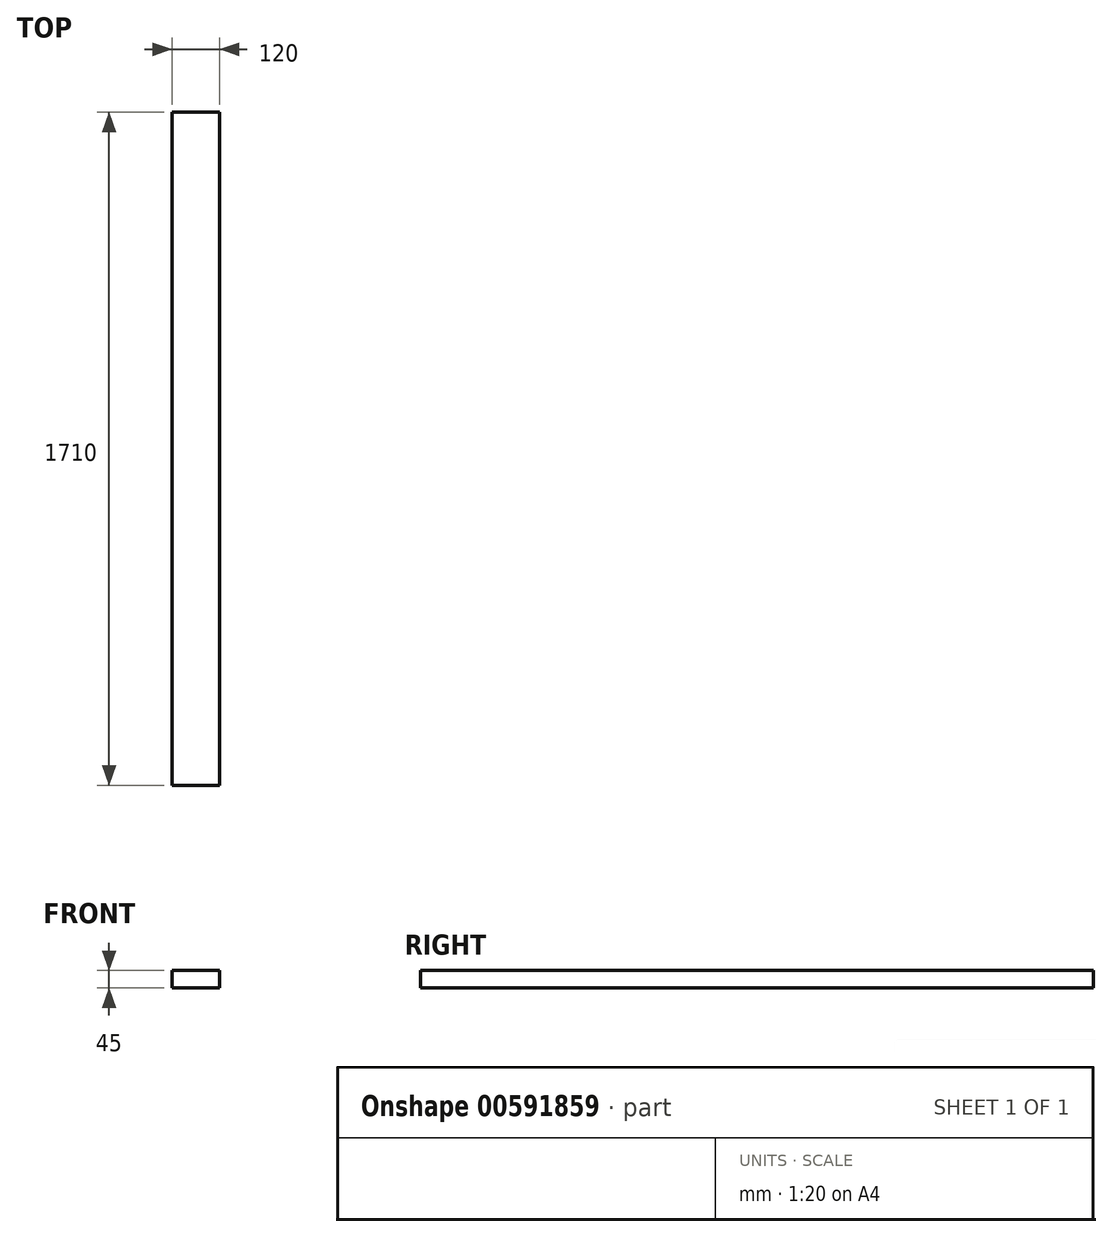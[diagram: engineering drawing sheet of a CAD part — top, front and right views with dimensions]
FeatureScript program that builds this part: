
annotation { "Feature Type Name" : "Feature", "Feature Type Description" : "" }
export const myFeature = defineFeature(function(context is Context, id is Id, definition is map)
    precondition{}
    {
        {
            var Q0;
            Q0=qCreatedBy(makeId("Top.planeOp"),FACE);
            var sketch = newSketch(context, id + "F0", { "sketchPlane" : qUnion([Q0])});
            skLineSegment(sketch, "E0.bottom", {"start": v(0, 0) * mm, "end": v(-120, 0) * mm});
            skLineSegment(sketch, "E0.top", {"start": v(0, 1710) * mm, "end": v(-120, 1710) * mm});
            skLineSegment(sketch, "E0.left", {"start": v(0, 0) * mm, "end": v(0, 1710) * mm});
            skLineSegment(sketch, "E0.right", {"start": v(-120, 0) * mm, "end": v(-120, 1710) * mm});
            skSolve(sketch);
        }
        {
            var Q0;
            Q0=makeQuery(id+"F0.imprint","IMPRINT",FACE,{"disambiguationData":[TD([[makeQuery(id+"F0.imprint","IMPRINT",EDGE,{"derivedFrom":sQuery(id+"F0.wireOp",EDGE,"E0.bottom")}),-1.0]])]});
            extrude(context, id + "F1", {"entities" : qUnion([Q0]), "depth" : 45 * mm, "offsetDistance" : 25 * mm});
        }
    });
